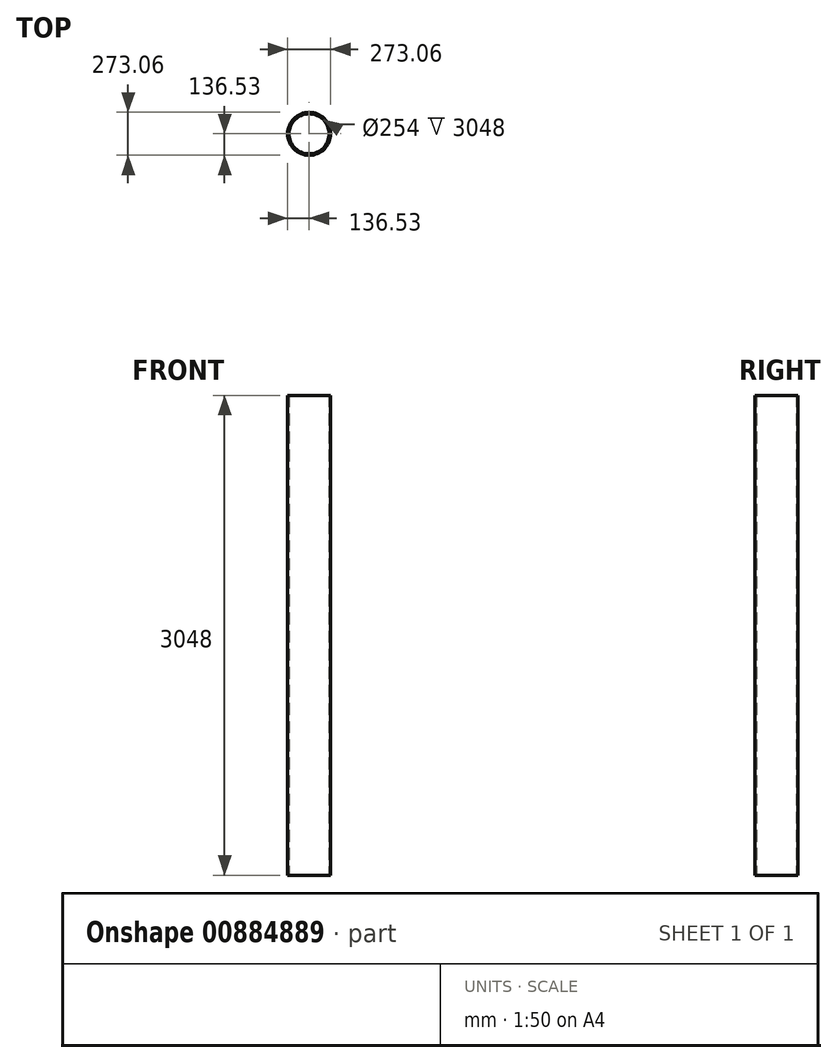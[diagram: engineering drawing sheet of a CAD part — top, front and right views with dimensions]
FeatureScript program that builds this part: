
annotation { "Feature Type Name" : "Feature", "Feature Type Description" : "" }
export const myFeature = defineFeature(function(context is Context, id is Id, definition is map)
    precondition{}
    {
        {
            var Q0;
            Q0=qCreatedBy(makeId("Top.planeOp"),FACE);
            var sketch = newSketch(context, id + "F0", { "sketchPlane" : qUnion([Q0])});
            skCircle(sketch, "E0", {"center": v(0, 0) * mm, "radius": 136.53 * mm});
            skCircle(sketch, "E1", {"center": v(0, 0) * mm, "radius": 127 * mm});
            skSolve(sketch);
        }
        {
            var Q0;
            Q0=makeQuery(id+"F0.imprint","IMPRINT",FACE,{"disambiguationData":[TD([[makeQuery(id+"F0.imprint","IMPRINT",EDGE,{"derivedFrom":sQuery(id+"F0.wireOp",EDGE,"E0")}),1.0]])]});
            extrude(context, id + "F1", {"entities" : qUnion([Q0]), "depth" : 3048 * mm, "offsetDistance" : 25.4 * mm});
        }
    });
